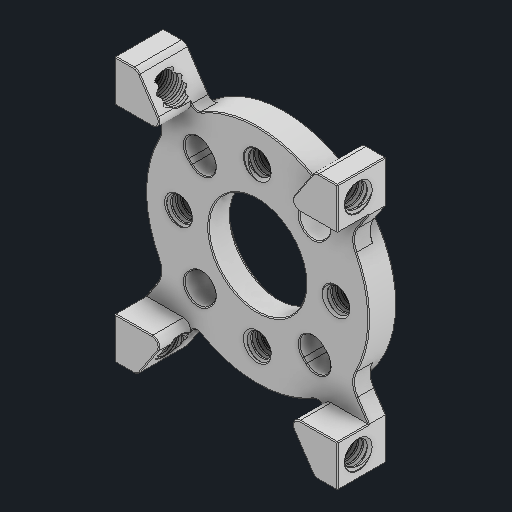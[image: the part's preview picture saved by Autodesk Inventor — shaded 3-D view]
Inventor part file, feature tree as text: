
AUTODESK INVENTOR PART (.ipt)
format: ipt  version: 2023 (Build 270158000, 158)  size: 2,272,768 bytes
history: native  units: in
note: dims shown in document units (in); Inventor stores cm internally (conversion verified against a paired STEP export)
features: chamfer x1
ambient origin geometry x8: Origin, YZ Plane, XZ Plane, XY Plane, X Axis, Y Axis, Z Axis, Center Point
bodies: Solid1 (feature_tree)
feature tree (1):
  chamfer  "Chamfer5"  [1 undecoded]
note: 1 required parameter value undecoded (feature->parameter linkage not recoverable at this tier; creation-order binding heuristic only, values carry confidence <= 0.55)
